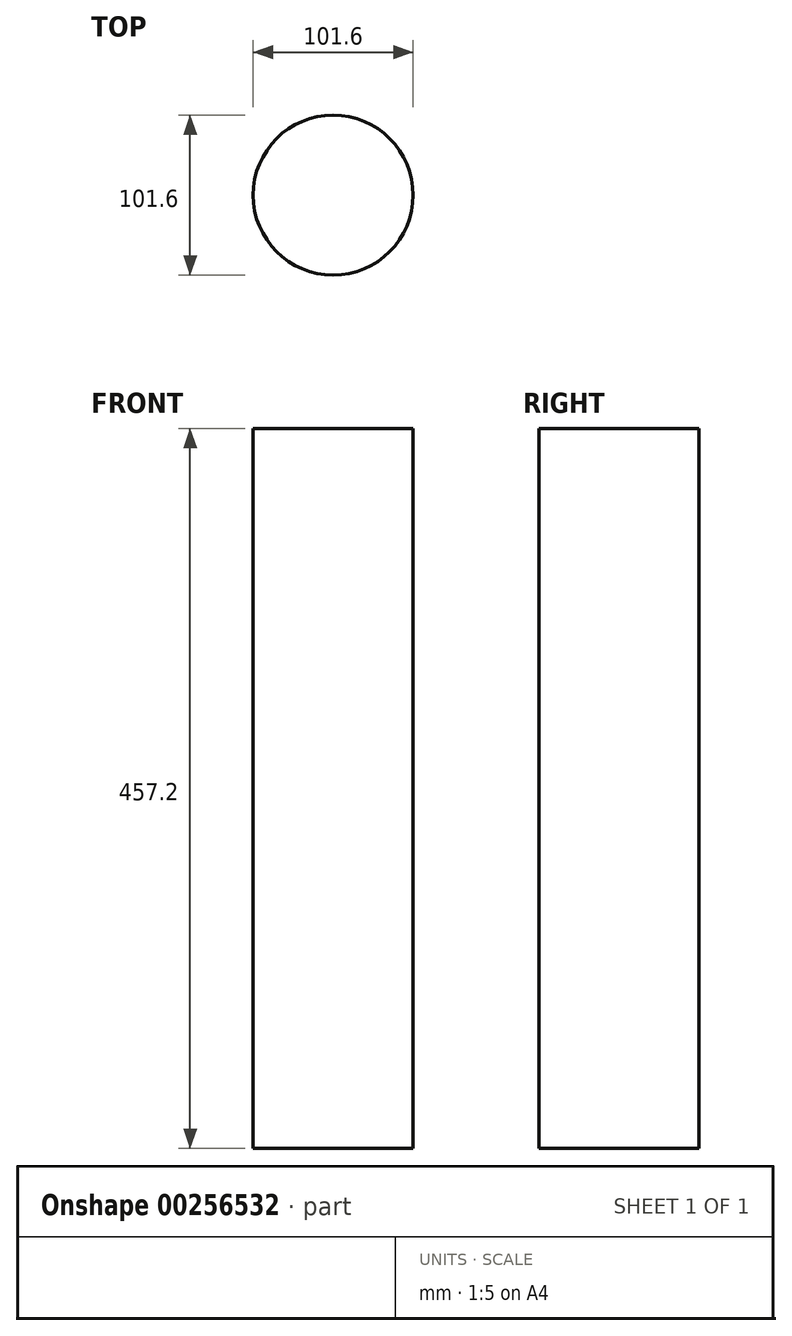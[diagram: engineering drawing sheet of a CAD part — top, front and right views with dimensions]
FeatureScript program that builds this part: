
annotation { "Feature Type Name" : "Feature", "Feature Type Description" : "" }
export const myFeature = defineFeature(function(context is Context, id is Id, definition is map)
    precondition{}
    {
        {
            var Q0;
            Q0=qCreatedBy(makeId("Top.planeOp"),FACE);
            var sketch = newSketch(context, id + "F0", { "sketchPlane" : qUnion([Q0])});
            skCircle(sketch, "E0", {"center": v(0, 0) * mm, "radius": 50.8 * mm});
            skSolve(sketch);
        }
        {
            var Q0;
            Q0=qSketchRegion(id+"F0",true);
            extrude(context, id + "F1", {"entities" : qUnion([Q0]), "depth" : 457.2 * mm});
        }
    });
